# Revit family: Thorn AVENUE F2 LED
name_source: partatom
category: Lighting Fixtures
revit_build: Autodesk Revit 2016 (Build: 20150220_1215(x64)
units: mm (PartAtom-declared; Revit-internal decimal feet)

## family parameters
Always vertical = Yes
Cut with Voids When Loaded = No
Light Source = Yes
OmniClass Number = 23.80.70.11
OmniClass Title = Luminaries for Internal Lighting
Part Type = Normal
Room Calculation Point = No
Round Connector Dimension = Use Diameter
Shared = No
Work Plane-Based = No

## types (1)
- AVN F2 LED
    Apparent Load = 21 VA
    Assembly Code = D5020210
    Body = Thorn_Metal_Dark_Grey
    Color Filter = 16777215
    Cover = Thorn_Glass_Self_llumination_Transparent
    Description = Outdoor luminaire
    Dimming Lamp Color Temperature Shift = <None>
    Emit Shape Visible in Rendering = No
    Emit from Circle Diameter = 201 mm  [stored 0.659449 ft]
    Height = 500 mm  [stored 1.64042 ft]
    Lamp = LED
    Length = 700 mm  [stored 2.29659 ft]
    Manufacturer = Thorn Lighting
    Model = 96260128
    Photometric Web File = 96260128_(STD).IES
    Tilt Angle = -90.00°
    URL = www.thornlighting.com/96260128
    Voltage = 230 V
    Width = 700 mm  [stored 2.29659 ft]

note: [stored X ft] marks values corroborated as IEEE doubles in the binary element streams (Revit-internal decimal feet)

## geometry (parser evidence)
native form markers: Blend x7, Sweep x1
no freeform markers — native parametric forms only
